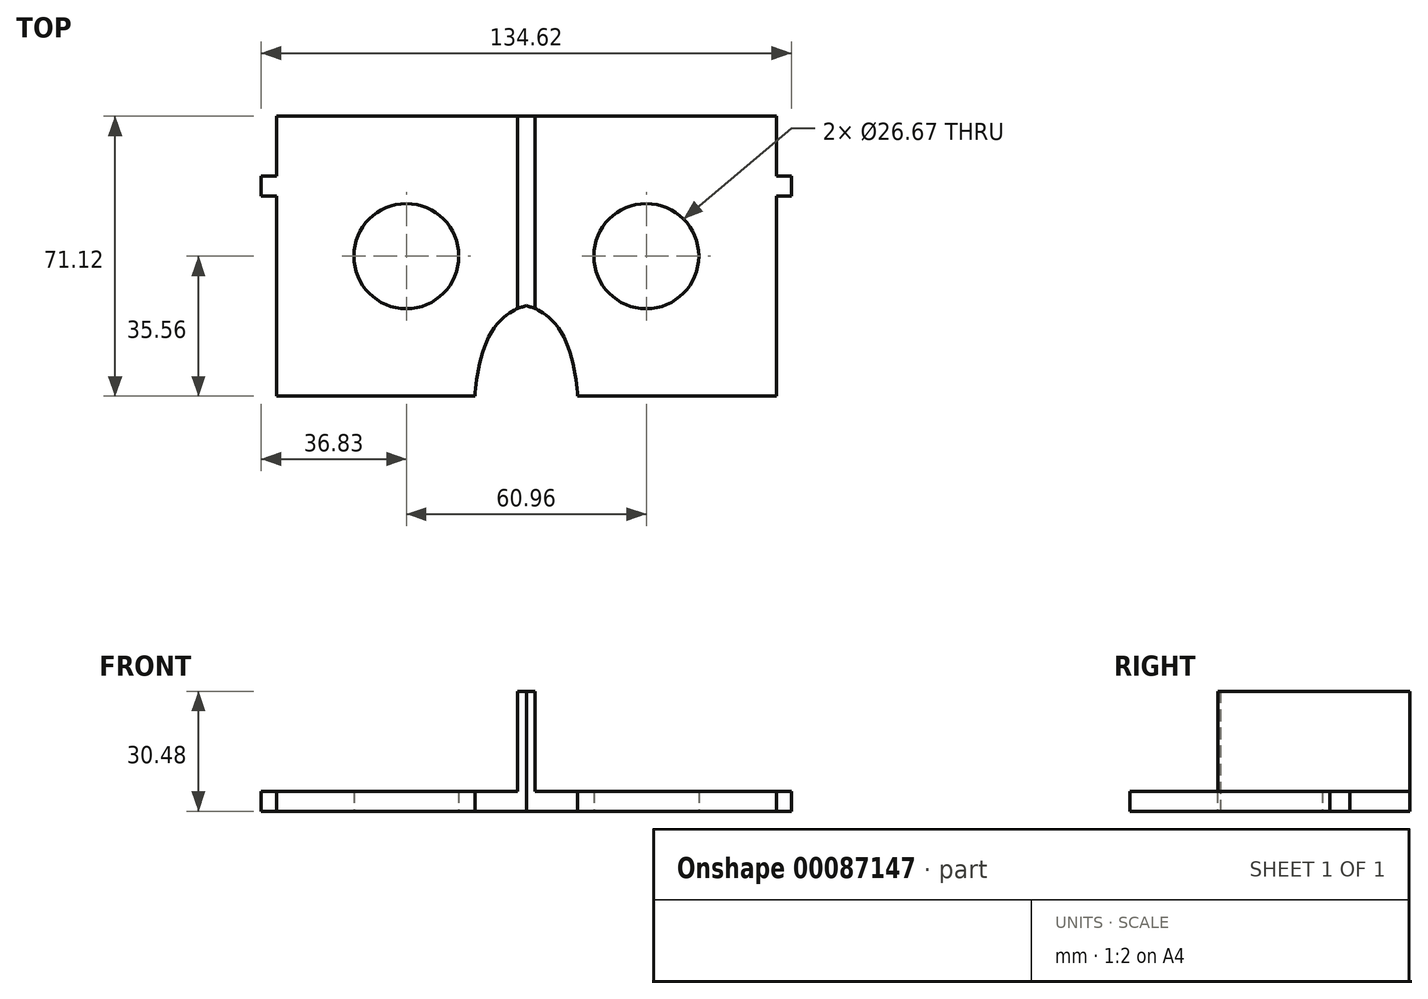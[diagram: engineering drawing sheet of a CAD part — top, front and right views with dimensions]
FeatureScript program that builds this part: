
annotation { "Feature Type Name" : "Feature", "Feature Type Description" : "" }
export const myFeature = defineFeature(function(context is Context, id is Id, definition is map)
    precondition{}
    {
        {
            var Q0;
            Q0=qCreatedBy(makeId("Top.planeOp"),FACE);
            var sketch = newSketch(context, id + "F0", { "sketchPlane" : qUnion([Q0])});
            skLineSegment(sketch, "E0.bottom", {"start": v(-63.5, -35.56) * mm, "end": v(-12.98, -35.56) * mm});
            skLineSegment(sketch, "E0.top", {"start": v(-63.5, 35.56) * mm, "end": v(63.5, 35.56) * mm});
            skLineSegment(sketch, "E0.left", {"start": v(-63.5, -35.56) * mm, "end": v(-63.5, 15.24) * mm});
            skLineSegment(sketch, "E0.right", {"start": v(63.5, -35.56) * mm, "end": v(63.5, 15.24) * mm});
            skPoint(sketch, "E0.middle", {"position": v(0, 0) * mm});
            skLineSegment(sketch, "E1", {"start": v(-63.5, 0) * mm, "end": v(-30.48, 0) * mm});
            skPoint(sketch, "E1.endSnap0", {"position": v(-63.5, 0) * mm});
            skCircle(sketch, "E2", {"center": v(-30.48, 0) * mm, "radius": 13.34 * mm});
            skCircle(sketch, "E3.MirrorC", {"center": v(30.48, 0) * mm, "radius": 13.34 * mm});
            skFitSpline(sketch, "E4", {"points": [v(-12.98, -35.56) * mm, v(-8.37, -18.52) * mm, v(-2.26, -13.26) * mm, v(0, -12.6) * mm], "startDerivative": vector(0, 22.73) * mm, "endDerivative": vector(37.86, 11.08) * mm});
            skFitSpline(sketch, "E5.MirrorCS", {"points": [v(12.98, -35.56) * mm, v(8.37, -18.52) * mm, v(2.26, -13.26) * mm, v(0, -12.6) * mm], "startDerivative": vector(0, 22.73) * mm, "endDerivative": vector(-37.86, 11.08) * mm});
            skLineSegment(sketch, "E6", {"start": v(-63.5, 0) * mm, "end": v(-63.5, 15.24) * mm});
            skLineSegment(sketch, "E7.bottom", {"start": v(-63.5, 15.24) * mm, "end": v(-67.31, 15.24) * mm});
            skLineSegment(sketch, "E7.top", {"start": v(-63.5, 20.32) * mm, "end": v(-67.31, 20.32) * mm});
            skLineSegment(sketch, "E7.right", {"start": v(-67.31, 15.24) * mm, "end": v(-67.31, 20.32) * mm});
            skPoint(sketch, "E7.middle", {"position": v(-63.5, 17.78) * mm});
            skPoint(sketch, "E7.left.end.orphan", {"position": v(-59.7, 20.32) * mm});
            skPoint(sketch, "E8.orphan", {"position": v(-59.7, 15.24) * mm});
            skLineSegment(sketch, "E9.trimOffspring", {"start": v(-63.5, 20.32) * mm, "end": v(-63.5, 35.56) * mm});
            skLineSegment(sketch, "E10.MirrorCS", {"start": v(63.5, 15.24) * mm, "end": v(67.31, 15.24) * mm});
            skLineSegment(sketch, "E11.MirrorCS", {"start": v(67.31, 15.24) * mm, "end": v(67.31, 20.32) * mm});
            skLineSegment(sketch, "E12.MirrorCS", {"start": v(63.5, 20.32) * mm, "end": v(67.3, 20.32) * mm});
            skLineSegment(sketch, "E13.trimOffspring", {"start": v(63.5, 20.32) * mm, "end": v(63.5, 35.56) * mm});
            skPoint(sketch, "E14.orphan", {"position": v(0, -35.56) * mm});
            skLineSegment(sketch, "E15.trimOffspring", {"start": v(12.98, -35.56) * mm, "end": v(63.5, -35.56) * mm});
            skLineSegment(sketch, "E16", {"start": v(-2.26, -13.26) * mm, "end": v(-2.26, 35.56) * mm});
            skLineSegment(sketch, "E17", {"start": v(2.26, -13.26) * mm, "end": v(2.26, 35.56) * mm});
            skSolve(sketch);
        }
        {
            var Q0;
            Q0 = qSketchRegion(id + "F0", true);
            extrude(context, id + "F1", {"entities" : qUnion([Q0]), "depth" : 5.08 * mm});
        }
        {
            var Q0;
            {var subQ0=sQuery(id+"F0.wireOp",EDGE,"E16");Q0=makeQuery(id+"F0.imprint","IMPRINT",FACE,{"disambiguationData":[TD([[makeQuery(id+"F0.imprint","IMPRINT",EDGE,{"derivedFrom":subQ0}),-1.0]])]});}
            extrude(context, id + "F2", {"entities" : qUnion([Q0]), "operationType" : NewBodyOperationType.ADD, "depth" : 30.48 * mm});
        }
    });
